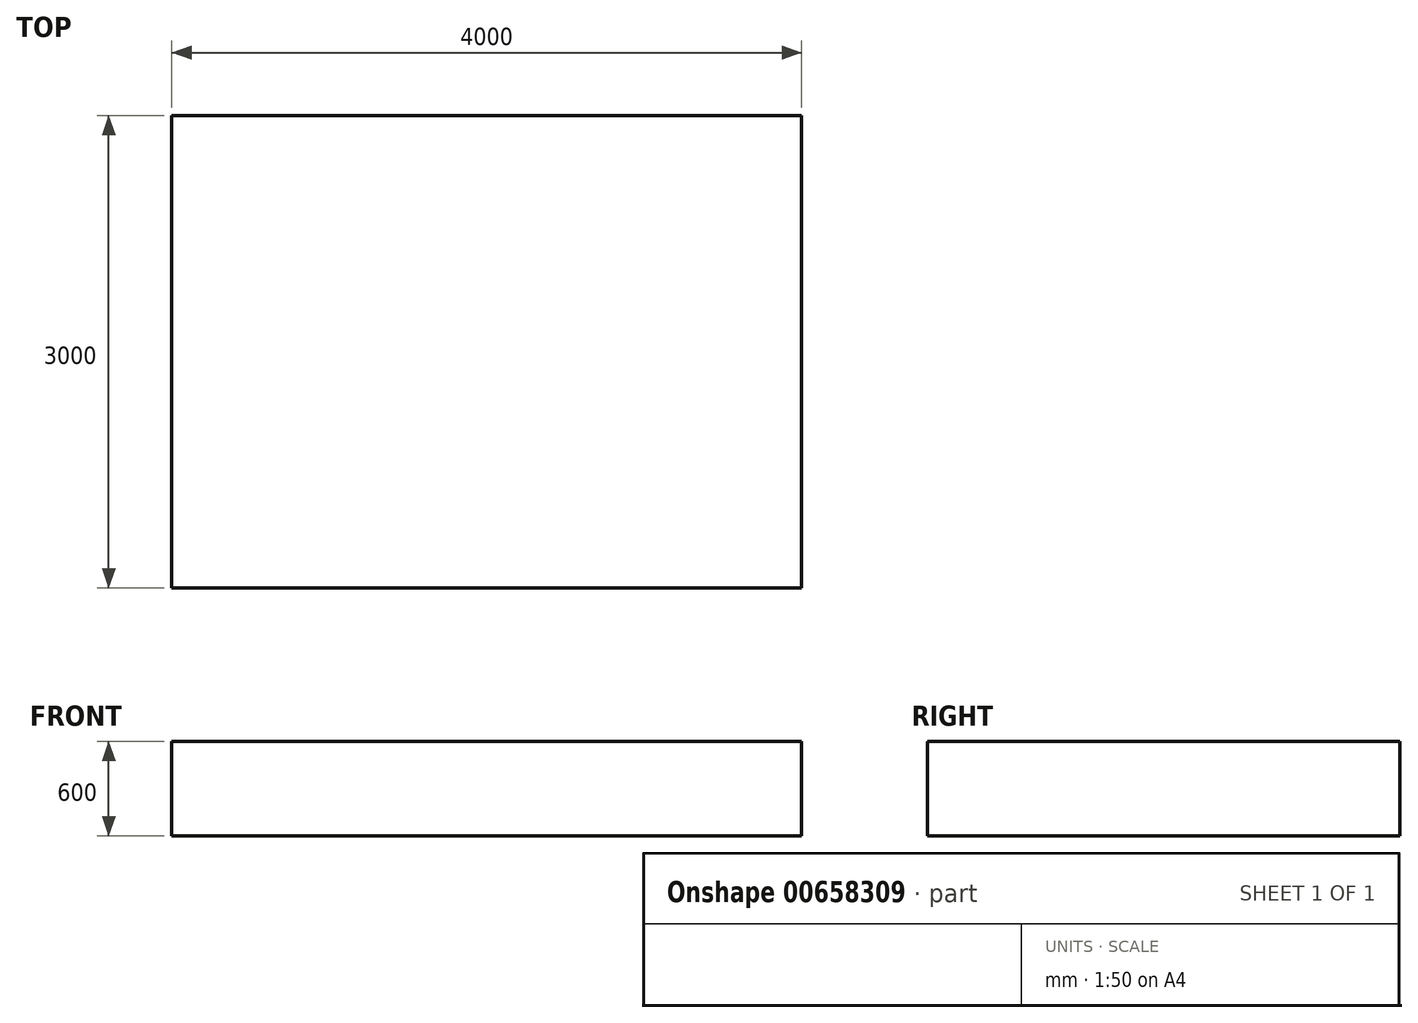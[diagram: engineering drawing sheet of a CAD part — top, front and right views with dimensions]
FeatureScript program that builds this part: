
annotation { "Feature Type Name" : "Feature", "Feature Type Description" : "" }
export const myFeature = defineFeature(function(context is Context, id is Id, definition is map)
    precondition{}
    {
        {
            var Q0;
            Q0=qCreatedBy(makeId("Top.planeOp"),FACE);
            var sketch = newSketch(context, id + "F0", { "sketchPlane" : qUnion([Q0])});
            skLineSegment(sketch, "E0.bottom", {"start": v(0, 0) * mm, "end": v(-2000, 0) * mm, "construction": true});
            skLineSegment(sketch, "E0.top", {"start": v(0, 1500) * mm, "end": v(-2000, 1500) * mm, "construction": true});
            skLineSegment(sketch, "E0.left", {"start": v(0, 0) * mm, "end": v(0, 1500) * mm, "construction": true});
            skLineSegment(sketch, "E0.right", {"start": v(-2000, 0) * mm, "end": v(-2000, 1500) * mm, "construction": true});
            skLineSegment(sketch, "E1.bottom", {"start": v(0, 0) * mm, "end": v(2000, 0) * mm, "construction": true});
            skLineSegment(sketch, "E1.top", {"start": v(0, 1500) * mm, "end": v(2000, 1500) * mm, "construction": true});
            skLineSegment(sketch, "E1.right", {"start": v(2000, 0) * mm, "end": v(2000, 1500) * mm, "construction": true});
            skLineSegment(sketch, "E2.top", {"start": v(0, -1500) * mm, "end": v(-2000, -1500) * mm, "construction": true});
            skLineSegment(sketch, "E2.left", {"start": v(0, 0) * mm, "end": v(0, -1500) * mm, "construction": true});
            skLineSegment(sketch, "E2.right", {"start": v(-2000, 0) * mm, "end": v(-2000, -1500) * mm, "construction": true});
            skLineSegment(sketch, "E3.top", {"start": v(0, -1500) * mm, "end": v(2000, -1500) * mm, "construction": true});
            skLineSegment(sketch, "E3.right", {"start": v(2000, 0) * mm, "end": v(2000, -1500) * mm, "construction": true});
            skLineSegment(sketch, "E4", {"start": v(-2000, 1500) * mm, "end": v(2000, -1500) * mm});
            skLineSegment(sketch, "E5", {"start": v(-2000, -1500) * mm, "end": v(2000, 1500) * mm});
            skLineSegment(sketch, "E6", {"start": v(-2000, 1500) * mm, "end": v(2000, 1500) * mm});
            skLineSegment(sketch, "E7", {"start": v(2000, 1500) * mm, "end": v(2000, -1500) * mm});
            skLineSegment(sketch, "E8", {"start": v(-2000, 1500) * mm, "end": v(-2000, -1500) * mm});
            skLineSegment(sketch, "E9", {"start": v(-2000, -1500) * mm, "end": v(2000, -1500) * mm});
            skSolve(sketch);
        }
        {
            var Q0;
            {var subQ0=sQuery(id+"F0.wireOp",EDGE,"E6");Q0=makeQuery(id+"F0.imprint","IMPRINT",FACE,{"disambiguationData":[TD([[makeQuery(id+"F0.imprint","IMPRINT",EDGE,{"derivedFrom":subQ0}),-1.0]])]});}
            var Q1;
            {var subQ0=sQuery(id+"F0.wireOp",EDGE,"E8");Q1=makeQuery(id+"F0.imprint","IMPRINT",FACE,{"disambiguationData":[TD([[makeQuery(id+"F0.imprint","IMPRINT",EDGE,{"derivedFrom":subQ0}),1.0]])]});}
            var Q2;
            {var subQ0=sQuery(id+"F0.wireOp",EDGE,"E9");Q2=makeQuery(id+"F0.imprint","IMPRINT",FACE,{"disambiguationData":[TD([[makeQuery(id+"F0.imprint","IMPRINT",EDGE,{"derivedFrom":subQ0}),1.0]])]});}
            var Q3;
            {var subQ0=sQuery(id+"F0.wireOp",EDGE,"E7");Q3=makeQuery(id+"F0.imprint","IMPRINT",FACE,{"disambiguationData":[TD([[makeQuery(id+"F0.imprint","IMPRINT",EDGE,{"derivedFrom":subQ0}),-1.0]])]});}
            extrude(context, id + "F1", {"entities" : qUnion([Q0, Q1, Q2, Q3]), "depth" : 600 * mm, "offsetDistance" : 25 * mm});
        }
    });
